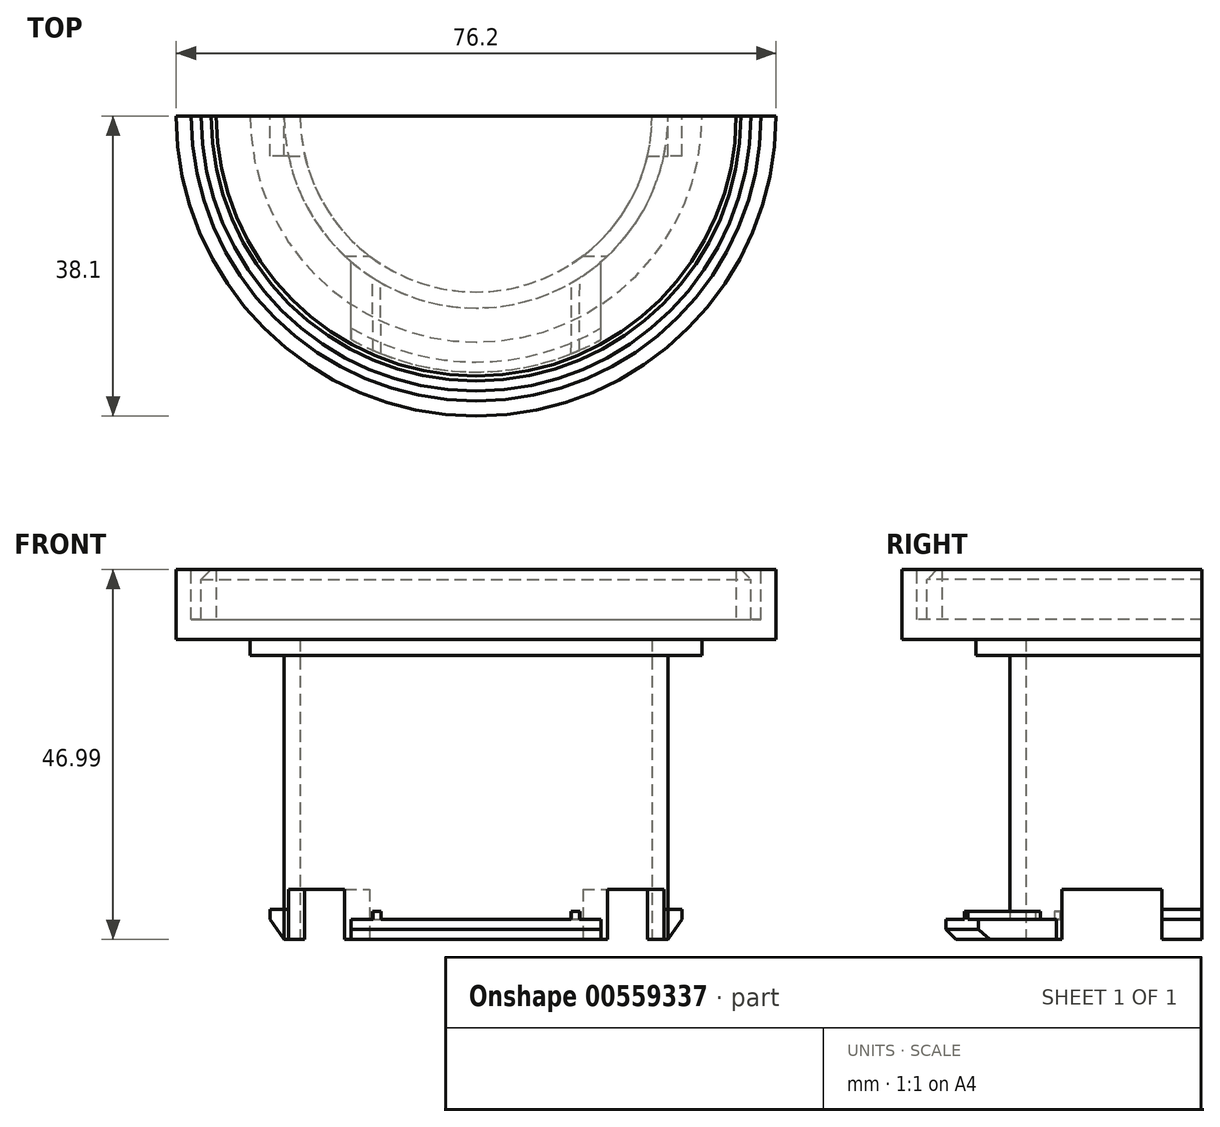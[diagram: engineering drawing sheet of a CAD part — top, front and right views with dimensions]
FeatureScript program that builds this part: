
annotation { "Feature Type Name" : "Feature", "Feature Type Description" : "" }
export const myFeature = defineFeature(function(context is Context, id is Id, definition is map)
    precondition{}
    {
        {
            var Q0;
            Q0=qCreatedBy(makeId("Top.planeOp"),FACE);
            var sketch = newSketch(context, id + "F0", { "sketchPlane" : qUnion([Q0])});
            skArc(sketch, "E0", {"start": v(-24.38, 0) * mm, "mid": v(0, -24.38) * mm, "end": v(24.38, 0) * mm});
            skArc(sketch, "E1.0", {"start": v(-22.35, 0) * mm, "mid": v(0, -22.35) * mm, "end": v(22.35, 0) * mm});
            skLineSegment(sketch, "E2", {"start": v(-24.38, 0) * mm, "end": v(-22.35, 0) * mm});
            skLineSegment(sketch, "E3", {"start": v(22.35, 0) * mm, "end": v(24.38, 0) * mm});
            skSolve(sketch);
        }
        {
            var Q0;
            Q0 = qSketchRegion(id + "F0", true);
            extrude(context, id + "F1", {"entities" : qUnion([Q0]), "depth" : 38.1 * mm, "offsetDistance" : 25.4 * mm});
        }
        {
            var Q0;
            Q0=makeQuery(id+"F1.opExtrude","CAP_FACE",FACE,{"disambiguationData":[OSD([sQuery(id+"F0.wireOp",EDGE,"E0"),sQuery(id+"F0.wireOp",EDGE,"E1.0"),sQuery(id+"F0.wireOp",EDGE,"E2"),sQuery(id+"F0.wireOp",EDGE,"E3")])],"isStart":false});
            var sketch = newSketch(context, id + "F2", { "sketchPlane" : qUnion([Q0])});
            skArc(sketch, "E4", {"start": v(-28.7, 0) * mm, "mid": v(0, -28.7) * mm, "end": v(28.7, 0) * mm});
            skLineSegment(sketch, "E5", {"start": v(-22.35, 0) * mm, "end": v(-28.7, 0) * mm});
            skLineSegment(sketch, "E6", {"start": v(22.35, 0) * mm, "end": v(28.7, 0) * mm});
            skArc(sketch, "E7", {"start": v(-22.35, 0) * mm, "mid": v(0, -22.35) * mm, "end": v(22.35, 0) * mm});
            skSolve(sketch);
        }
        {
            var Q0;
            Q0 = qSketchRegion(id + "F2", true);
            extrude(context, id + "F3", {"entities" : qUnion([Q0]), "operationType" : NewBodyOperationType.ADD, "oppositeDirection" : true, "depth" : 2.03 * mm, "offsetDistance" : 25.4 * mm});
        }
        {
            var Q0;
            Q0=makeQuery(id+"F1.opExtrude","CAP_FACE",FACE,{"disambiguationData":[OSD([sQuery(id+"F0.wireOp",EDGE,"E0"),sQuery(id+"F0.wireOp",EDGE,"E1.0"),sQuery(id+"F0.wireOp",EDGE,"E2"),sQuery(id+"F0.wireOp",EDGE,"E3")])],"isStart":true});
            var sketch = newSketch(context, id + "F4", { "sketchPlane" : qUnion([Q0])});
            skArc(sketch, "E8", {"start": v(15.87, 28.37) * mm, "mid": v(0, 32.51) * mm, "end": v(-15.87, 28.37) * mm});
            skLineSegment(sketch, "E9", {"start": v(-15.87, 28.37) * mm, "end": v(-15.88, 18.21) * mm});
            skLineSegment(sketch, "E10", {"start": v(15.87, 28.37) * mm, "end": v(15.88, 18.21) * mm});
            skArc(sketch, "E11", {"start": v(15.87, 18.21) * mm, "mid": v(0, 24.16) * mm, "end": v(-15.87, 18.21) * mm});
            skSolve(sketch);
        }
        {
            var Q0;
            Q0 = qSketchRegion(id + "F4", true);
            extrude(context, id + "F5", {"entities" : qUnion([Q0]), "operationType" : NewBodyOperationType.ADD, "oppositeDirection" : true, "depth" : 2.54 * mm, "offsetDistance" : 25.4 * mm});
        }
        {
            var Q0;
            Q0=makeQuery(id+"F5.opExtrude","CAP_FACE",FACE,{"disambiguationData":[OSD([sQuery(id+"F4.wireOp",EDGE,"E8"),sQuery(id+"F4.wireOp",EDGE,"E9"),sQuery(id+"F4.wireOp",EDGE,"E10"),sQuery(id+"F4.wireOp",EDGE,"E11")])],"isStart":false});
            var sketch = newSketch(context, id + "F6", { "sketchPlane" : qUnion([Q0])});
            skLineSegment(sketch, "E12.top", {"start": v(-11.93, 105.28) * mm, "end": v(-13.1, 105.28) * mm});
            skLineSegment(sketch, "E12.left", {"start": v(-12.08, -30.18) * mm, "end": v(-12.16, -18.75) * mm});
            skLineSegment(sketch, "E12.right", {"start": v(-13.1, -29.76) * mm, "end": v(-13.19, -18.05) * mm});
            skLineSegment(sketch, "E13", {"start": v(-13.1, -29.76) * mm, "end": v(-12.08, -30.18) * mm});
            skLineSegment(sketch, "E14", {"start": v(-13.19, -18.05) * mm, "end": v(-12.16, -18.75) * mm});
            skLineSegment(sketch, "E15.MirrorCS", {"start": v(13.1, -29.76) * mm, "end": v(13.19, -18.05) * mm});
            skLineSegment(sketch, "E16.MirrorCS", {"start": v(12.08, -30.18) * mm, "end": v(12.16, -18.75) * mm});
            skLineSegment(sketch, "E17.MirrorCS", {"start": v(13.19, -18.05) * mm, "end": v(12.16, -18.75) * mm});
            skLineSegment(sketch, "E18.MirrorCS", {"start": v(13.1, -29.76) * mm, "end": v(12.08, -30.18) * mm});
            skSolve(sketch);
        }
        {
            var Q0;
            Q0 = qSketchRegion(id + "F6", true);
            extrude(context, id + "F7", {"entities" : qUnion([Q0]), "operationType" : NewBodyOperationType.ADD, "depth" : 1.02 * mm, "offsetDistance" : 25.4 * mm});
        }
        {
            var Q0;
            Q0=qCreatedBy(makeId("Right.planeOp"),FACE);
            var sketch = newSketch(context, id + "F8", { "sketchPlane" : qUnion([Q0])});
            skLineSegment(sketch, "E19.bottom", {"start": v(-5.08, 6.35) * mm, "end": v(-17.78, 6.35) * mm});
            skLineSegment(sketch, "E19.top", {"start": v(-5.08, 0) * mm, "end": v(-17.78, 0) * mm});
            skLineSegment(sketch, "E19.left", {"start": v(-5.08, 6.35) * mm, "end": v(-5.08, 0) * mm});
            skLineSegment(sketch, "E19.right", {"start": v(-17.78, 6.35) * mm, "end": v(-17.78, 0) * mm});
            skSolve(sketch);
        }
        {
            var Q0;
            Q0 = qSketchRegion(id + "F8", true);
            extrude(context, id + "F9", {"entities" : qUnion([Q0]), "operationType" : NewBodyOperationType.REMOVE, "endBound" : BoundingType.SYMMETRIC, "oppositeDirection" : true, "depth" : 76.2 * mm, "offsetDistance" : 25.4 * mm});
        }
        {
            var Q0;
            Q0=makeQuery(id+"F3.boolean.opBoolean","MERGE",FACE,{"derivedFrom":[makeQuery(id+"F1.opExtrude","SWEPT_FACE",FACE,{"disambiguationData":[OSD([sQuery(id+"F0.wireOp",EDGE,"E2")])]}),makeQuery(id+"F3.opExtrude","SWEPT_FACE",FACE,{"disambiguationData":[OSD([sQuery(id+"F2.wireOp",EDGE,"E5")])]})]});
            var sketch = newSketch(context, id + "F10", { "sketchPlane" : qUnion([Q0])});
            skLineSegment(sketch, "E20", {"start": v(24.38, 0) * mm, "end": v(24.38, 3.81) * mm});
            skLineSegment(sketch, "E21", {"start": v(24.38, 3.81) * mm, "end": v(26.16, 3.81) * mm});
            skLineSegment(sketch, "E22", {"start": v(26.16, 3.81) * mm, "end": v(26.16, 2.54) * mm});
            skLineSegment(sketch, "E23", {"start": v(26.16, 2.54) * mm, "end": v(24.38, 0) * mm});
            skLineSegment(sketch, "E24.MirrorCS", {"start": v(-24.38, 0) * mm, "end": v(-24.38, 3.81) * mm});
            skLineSegment(sketch, "E25.MirrorCS", {"start": v(-24.38, 3.81) * mm, "end": v(-26.16, 3.81) * mm});
            skLineSegment(sketch, "E26.MirrorCS", {"start": v(-26.16, 3.81) * mm, "end": v(-26.16, 2.54) * mm});
            skLineSegment(sketch, "E27.MirrorCS", {"start": v(-26.16, 2.54) * mm, "end": v(-24.38, 0) * mm});
            skSolve(sketch);
        }
        {
            var Q0;
            Q0 = qSketchRegion(id + "F10", true);
            extrude(context, id + "F11", {"entities" : qUnion([Q0]), "oppositeDirection" : true, "depth" : 5.08 * mm, "offsetDistance" : 25.4 * mm});
        }
        {
            var Q0;
            Q0=makeQuery(id+"F11.opExtrude","SWEPT_FACE",FACE,{"disambiguationData":[OSD([sQuery(id+"F10.wireOp",EDGE,"E20")])]});
            var sketch = newSketch(context, id + "F12", { "sketchPlane" : qUnion([Q0])});
            skLineSegment(sketch, "E28.bottom", {"start": v(-5.08, 0) * mm, "end": v(0, 0) * mm});
            skLineSegment(sketch, "E28.top", {"start": v(-5.08, 3.81) * mm, "end": v(0, 3.81) * mm});
            skLineSegment(sketch, "E28.left", {"start": v(-5.08, 0) * mm, "end": v(-5.08, 3.81) * mm});
            skLineSegment(sketch, "E28.right", {"start": v(0, 0) * mm, "end": v(0, 3.81) * mm});
            skSolve(sketch);
        }
        {
            var Q0;
            Q0 = qSketchRegion(id + "F12", true);
            var Q1;
            Q1=makeQuery(id+"F1.opExtrude","SWEPT_FACE",FACE,{"disambiguationData":[OSD([sQuery(id+"F0.wireOp",EDGE,"E0")])]});
            extrude(context, id + "F13", {"entities" : qUnion([Q0]), "endBound" : BoundingType.UP_TO_SURFACE, "depth" : 25.4 * mm, "endBoundEntityFace" : qUnion([Q1]), "offsetDistance" : 25.4 * mm});
        }
        {
            var Q0;
            Q0=makeQuery(id+"F11.opExtrude","SWEPT_FACE",FACE,{"disambiguationData":[OSD([sQuery(id+"F10.wireOp",EDGE,"E24.MirrorCS")])]});
            var sketch = newSketch(context, id + "F14", { "sketchPlane" : qUnion([Q0])});
            skLineSegment(sketch, "E29.bottom", {"start": v(5.08, 0) * mm, "end": v(0, 0) * mm});
            skLineSegment(sketch, "E29.top", {"start": v(5.08, 3.81) * mm, "end": v(0, 3.8) * mm});
            skLineSegment(sketch, "E29.left", {"start": v(5.08, 0) * mm, "end": v(5.08, 3.81) * mm});
            skLineSegment(sketch, "E29.right", {"start": v(0, 0) * mm, "end": v(0, 3.81) * mm});
            skSolve(sketch);
        }
        {
            var Q0;
            Q0 = qSketchRegion(id + "F14", true);
            var Q1;
            Q1=makeQuery(id+"F1.opExtrude","SWEPT_FACE",FACE,{"disambiguationData":[OSD([sQuery(id+"F0.wireOp",EDGE,"E0")])]});
            extrude(context, id + "F15", {"entities" : qUnion([Q0]), "endBound" : BoundingType.UP_TO_SURFACE, "depth" : 25.4 * mm, "endBoundEntityFace" : qUnion([Q1]), "offsetDistance" : 25.4 * mm});
        }
        {
            var Q0;
            Q0=makeQuery(id+"F3.boolean.opBoolean","MERGE",FACE,{"derivedFrom":[makeQuery(id+"F1.opExtrude","CAP_FACE",FACE,{"disambiguationData":[OSD([sQuery(id+"F0.wireOp",EDGE,"E0"),sQuery(id+"F0.wireOp",EDGE,"E1.0"),sQuery(id+"F0.wireOp",EDGE,"E2"),sQuery(id+"F0.wireOp",EDGE,"E3")])],"isStart":false}),makeQuery(id+"F3.opExtrude","CAP_FACE",FACE,{"disambiguationData":[OSD([sQuery(id+"F2.wireOp",EDGE,"E4"),sQuery(id+"F2.wireOp",EDGE,"E5"),sQuery(id+"F2.wireOp",EDGE,"E6"),sQuery(id+"F2.wireOp",EDGE,"E7")])],"isStart":true})]});
            var sketch = newSketch(context, id + "F16", { "sketchPlane" : qUnion([Q0])});
            skArc(sketch, "E30", {"start": v(-38.1, 0) * mm, "mid": v(0, -38.1) * mm, "end": v(38.1, 0) * mm});
            skLineSegment(sketch, "E31", {"start": v(-38.1, 0) * mm, "end": v(38.1, 0) * mm});
            skSolve(sketch);
        }
        {
            var Q0;
            Q0 = qSketchRegion(id + "F16", true);
            extrude(context, id + "F17", {"entities" : qUnion([Q0]), "operationType" : NewBodyOperationType.ADD, "depth" : 2.54 * mm, "offsetDistance" : 25.4 * mm});
        }
        {
            var Q0;
            Q0=makeQuery(id+"F17.opExtrude","CAP_FACE",FACE,{"disambiguationData":[OSD([sQuery(id+"F16.wireOp",EDGE,"E30"),sQuery(id+"F16.wireOp",EDGE,"E31")])],"isStart":false});
            var sketch = newSketch(context, id + "F18", { "sketchPlane" : qUnion([Q0])});
            skArc(sketch, "E32", {"start": v(-38.1, 0) * mm, "mid": v(0, -38.1) * mm, "end": v(38.1, 0) * mm});
            skArc(sketch, "E33.0", {"start": v(-33.02, 0) * mm, "mid": v(0, -33.02) * mm, "end": v(33.02, 0) * mm});
            skLineSegment(sketch, "E34", {"start": v(-38.1, 0) * mm, "end": v(-33.02, 0) * mm});
            skLineSegment(sketch, "E35", {"start": v(33.02, 0) * mm, "end": v(38.1, 0) * mm});
            skSolve(sketch);
        }
        {
            var Q0;
            Q0 = qSketchRegion(id + "F18", true);
            extrude(context, id + "F19", {"entities" : qUnion([Q0]), "operationType" : NewBodyOperationType.ADD, "depth" : 6.35 * mm, "offsetDistance" : 25.4 * mm});
        }
        {
            var Q0;
            Q0=makeQuery(id+"F19.opExtrude","CAP_FACE",FACE,{"disambiguationData":[OSD([sQuery(id+"F18.wireOp",EDGE,"E32"),sQuery(id+"F18.wireOp",EDGE,"E33.0"),sQuery(id+"F18.wireOp",EDGE,"E34"),sQuery(id+"F18.wireOp",EDGE,"E35")])],"isStart":false});
            var sketch = newSketch(context, id + "F20", { "sketchPlane" : qUnion([Q0])});
            skArc(sketch, "E36", {"start": v(-36.2, 0) * mm, "mid": v(0, -36.2) * mm, "end": v(36.2, 0) * mm});
            skArc(sketch, "E37", {"start": v(-34.93, 0) * mm, "mid": v(0, -34.93) * mm, "end": v(34.93, 0) * mm});
            skLineSegment(sketch, "E38", {"start": v(34.93, 0) * mm, "end": v(36.2, 0) * mm});
            skLineSegment(sketch, "E39", {"start": v(-36.2, 0) * mm, "end": v(-34.93, 0) * mm});
            skSolve(sketch);
        }
        {
            var Q0;
            Q0 = qSketchRegion(id + "F20", true);
            var Q1;
            Q1=makeQuery(id+"F17.opExtrude","CAP_FACE",FACE,{"disambiguationData":[OSD([sQuery(id+"F16.wireOp",EDGE,"E30"),sQuery(id+"F16.wireOp",EDGE,"E31")])],"isStart":false});
            extrude(context, id + "F21", {"entities" : qUnion([Q0]), "operationType" : NewBodyOperationType.REMOVE, "endBound" : BoundingType.UP_TO_SURFACE, "oppositeDirection" : true, "depth" : 25.4 * mm, "endBoundEntityFace" : qUnion([Q1]), "offsetDistance" : 25.4 * mm});
        }
        {
            var Q0;
            Q0=makeQuery(id+"F21.boolean.opBoolean","COPY",EDGE,{"derivedFrom":makeQuery(id+"F21.opExtrude","CAP_EDGE",EDGE,{"disambiguationData":[OSD([sQuery(id+"F20.wireOp",EDGE,"E37")])],"isStart":true})});
            var Q1;
            Q1=makeQuery(id+"F21.boolean.opBoolean","COPY",EDGE,{"derivedFrom":makeQuery(id+"F21.opExtrude","CAP_EDGE",EDGE,{"disambiguationData":[OSD([sQuery(id+"F20.wireOp",EDGE,"E36")])],"isStart":true})});
            var Q2;
            Q2=makeQuery(id+"F5.opExtrude","CAP_EDGE",EDGE,{"disambiguationData":[OSD([sQuery(id+"F4.wireOp",EDGE,"E8")])],"isStart":true});
            chamfer(context, id + "F22", {"entities" : qUnion([Q0, Q1, Q2]), "width" : 1.27 * mm, "tangentPropagation" : true});
        }
    });
